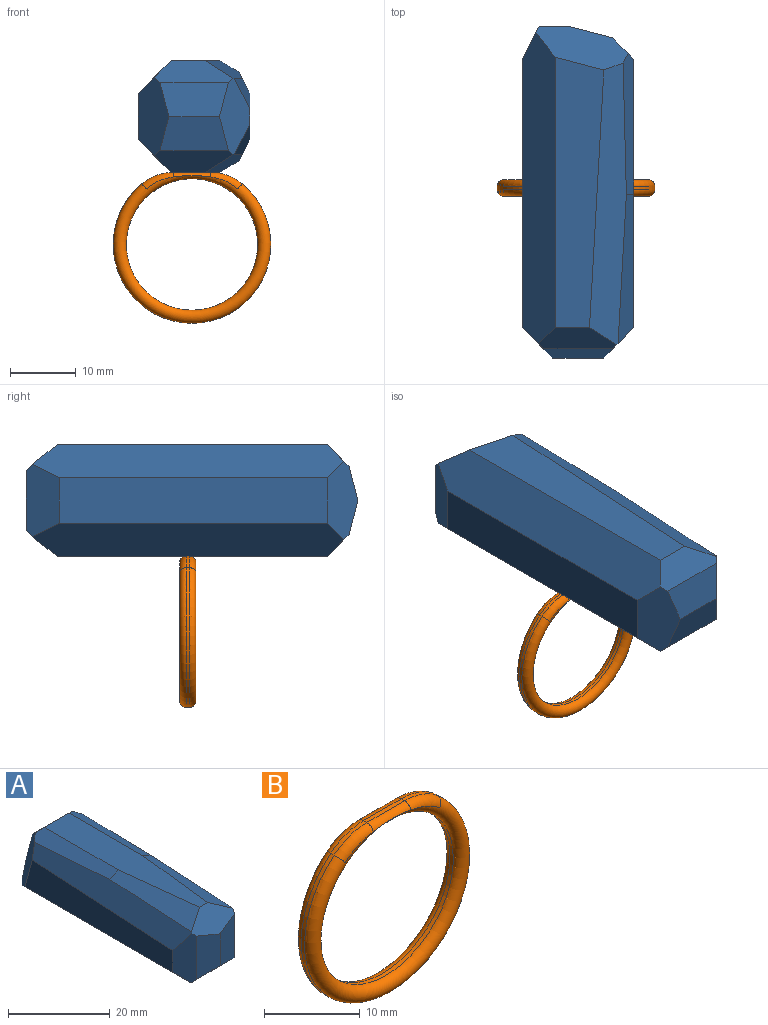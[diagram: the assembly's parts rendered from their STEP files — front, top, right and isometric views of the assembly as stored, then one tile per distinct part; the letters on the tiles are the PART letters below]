
ASSEMBLY  parts=2 mates=1
PART A: 27 faces, bbox 17x50.6x17 mm
  f0: plane 40.84x7mm, normal (0,0,-1), area 285.9mm2, adj f8,f13,f14,f17
  f1: plane 41.15x7.42mm, normal (1,0,0), area 255.1mm2, adj f6,f12,f13,f15
  f2: plane 40.84x6.84mm, normal (0,0,1), area 233.2mm2, adj f4,f5,f7,f9,f21,f22
  f3: plane 9.01x4.3mm, normal (0,1,0), area 34.1mm2, adj f10,f14,f15,f16
  f4: plane 21.38x3.31mm, normal (0.45,0,0.89), area 65.9mm2, adj f2,f5,f7,f12,f15
  f5: plane 22.75x4.59mm, normal (0.45,-0.05,0.89), area 84.7mm2, adj f2,f4,f9,f12
  f6: plane 11.86x3.28mm, normal (0.71,-0.71,0), area 42.2mm2, adj f1,f8,f9,f11,f12,f13
  f7: plane 10.3x3.28mm, normal (0,0.71,0.71), area 39.8mm2, adj f2,f4,f10,f15,f16,f22
  f8: plane 12x4.65mm, normal (0,-0.71,-0.71), area 56.1mm2, adj f0,f6,f11,f13,f17,f19,f20
  f9: plane 11.72x4.65mm, normal (0,-0.71,0.71), area 47.2mm2, adj f2,f5,f6,f11,f12,f18,f19,f20
  f10: plane 6.88x6.84mm, normal (0,0.97,0.25), area 48.6mm2, adj f3,f7,f15,f16
  f11: plane 10.43x5.22mm, normal (0.25,-0.97,0), area 48.9mm2, adj f6,f8,f9,f19
  f12: plane 42.92x5.62mm, normal (0.85,-0.03,0.53), area 198.7mm2, adj f1,f4,f5,f6,f9,f15
  f13: plane 47.46x5mm, normal (0.71,0,-0.71), area 312.8mm2, adj f0,f1,f6,f8,f14,f15
  f14: plane 11.12x5.08mm, normal (0,0.45,-0.89), area 52.5mm2, adj f0,f3,f13,f15,f16,f17
  f15: plane 14.08x6.71mm, normal (0.71,0.68,0.18), area 83.8mm2, adj f1,f3,f4,f7,f10,f12,f13,f14
  f16: plane 14.08x6.71mm, normal (-0.71,0.68,0.18), area 83.8mm2, adj f3,f7,f10,f14,f17,f18,f22,f23
  f17: plane 47.46x5mm, normal (-0.71,0,-0.71), area 312.8mm2, adj f0,f8,f14,f16,f20,f23
  f18: plane 42.92x5.62mm, normal (-0.85,-0.03,0.53), area 198.7mm2, adj f9,f16,f20,f21,f22,f23
  f19: plane 10.43x5.22mm, normal (-0.25,-0.97,0), area 48.9mm2, adj f8,f9,f11,f20
  f20: plane 11.86x3.28mm, normal (-0.71,-0.71,0), area 42.2mm2, adj f8,f9,f17,f18,f19,f23
  f21: plane 22.75x4.59mm, normal (-0.45,-0.05,0.89), area 84.7mm2, adj f2,f9,f18,f22
  f22: plane 21.38x3.31mm, normal (-0.45,0,0.89), area 65.9mm2, adj f2,f7,f16,f18,f21
  f23: plane 41.15x7.42mm, normal (-1,0,0), area 255.1mm2, adj f16,f17,f18,f20
  f24: plane 15x15mm, normal (0,1,0), area 176.7mm2, adj f26
  f25: plane 15x15mm, normal (0,-1,0), area 176.7mm2, adj f26
  f26: cylinder r=7.5mm len=40mm, axis (0,1,0), area 1885mm2, adj f24,f25
PART B: 13 faces, bbox 26x2.5x26 mm
  f0: plane 5.57x0.5mm, normal (0,0,1), area 2.8mm2, adj f3,f4,f8,f12
  f1: cylinder r=10mm len=20mm, axis (0,1,0), area 31.4mm2, adj f5,f9
  f2: cylinder r=12mm len=24mm, axis (0,1,0), area 29.4mm2, adj f3,f4,f5,f9
  f3: cylinder r=7.62mm len=4.85mm, axis (0,1,0), area 2.6mm2, adj f0,f2,f7,f10
  f4: cylinder r=7.62mm len=4.85mm, axis (0,1,0), area 2.6mm2, adj f0,f2,f6,f11
  f5: torus R=11mm, axis (0,-1,0), area 187.9mm2, adj f1,f2,f6,f7,f8
  f6: torus R=6.62mm, axis (0,-1,0), area 7.1mm2, adj f4,f5,f8
  f7: torus R=6.62mm, axis (0,-1,0), area 7.1mm2, adj f3,f5,f8
  f8: cylinder r=1mm len=5.57mm, axis (1,0,0), area 6.2mm2, adj f0,f5,f6,f7
  f9: torus R=11mm, axis (0,-1,0), area 187.9mm2, adj f1,f2,f10,f11,f12
  f10: torus R=6.62mm, axis (0,-1,0), area 7.1mm2, adj f3,f9,f12
  f11: torus R=6.62mm, axis (0,-1,0), area 7.1mm2, adj f4,f9,f12
  f12: cylinder r=1mm len=5.57mm, axis (-1,0,0), area 6.2mm2, adj f0,f9,f10,f11
PLACE A rot(axis=(0,1,0),90deg) t=(49.41,26.26,21.03)mm
PLACE B t=(49.08,28.87,1.53)mm
MATE fastened A.f1 <-> B.f0  axis (0,0,-1) through (49.08,27.62,12.53)mm
